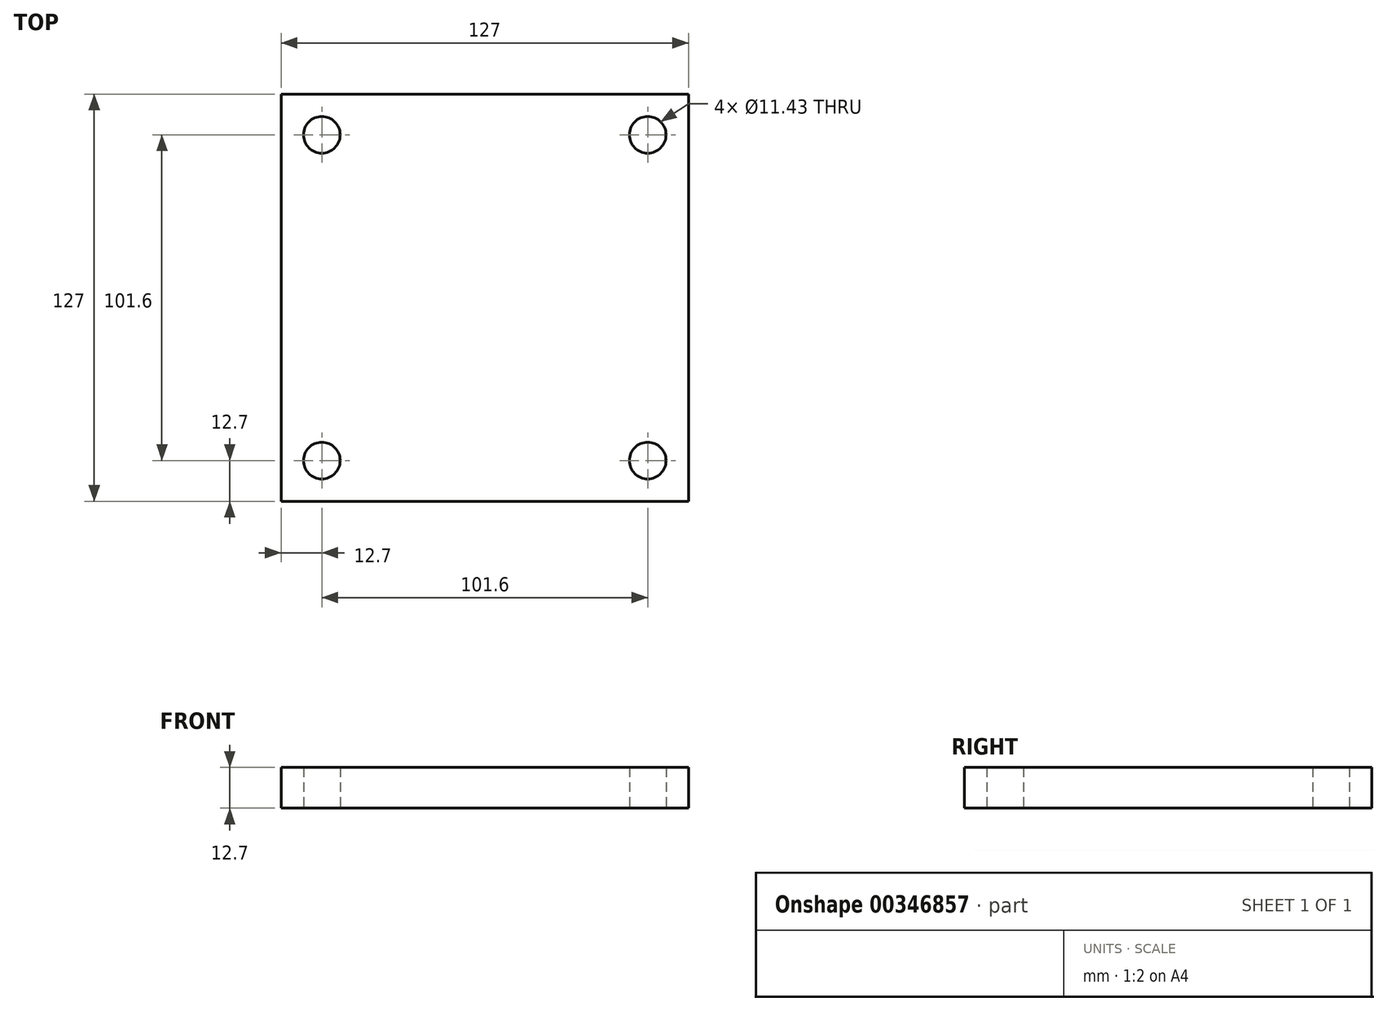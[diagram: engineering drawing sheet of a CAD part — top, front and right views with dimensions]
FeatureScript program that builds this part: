
annotation { "Feature Type Name" : "Feature", "Feature Type Description" : "" }
export const myFeature = defineFeature(function(context is Context, id is Id, definition is map)
    precondition{}
    {
        {
            var Q0;
            Q0=qCreatedBy(makeId("Top.planeOp"),FACE);
            var sketch = newSketch(context, id + "F0", { "sketchPlane" : qUnion([Q0])});
            skLineSegment(sketch, "E0.bottom", {"start": v(63.5, 63.5) * mm, "end": v(-63.5, 63.5) * mm});
            skLineSegment(sketch, "E0.top", {"start": v(63.5, -63.5) * mm, "end": v(-63.5, -63.5) * mm});
            skLineSegment(sketch, "E0.left", {"start": v(63.5, 63.5) * mm, "end": v(63.5, -63.5) * mm});
            skLineSegment(sketch, "E0.right", {"start": v(-63.5, 63.5) * mm, "end": v(-63.5, -63.5) * mm});
            skPoint(sketch, "E0.middle", {"position": v(0, 0) * mm});
            skLineSegment(sketch, "E1.bottom", {"start": v(50.8, 50.8) * mm, "end": v(-50.8, 50.8) * mm});
            skLineSegment(sketch, "E1.top", {"start": v(50.8, -50.8) * mm, "end": v(-50.8, -50.8) * mm});
            skLineSegment(sketch, "E1.left", {"start": v(50.8, 50.8) * mm, "end": v(50.8, -50.8) * mm});
            skLineSegment(sketch, "E1.right", {"start": v(-50.8, 50.8) * mm, "end": v(-50.8, -50.8) * mm});
            skCircle(sketch, "E2", {"center": v(-50.8, 50.8) * mm, "radius": 5.72 * mm});
            skCircle(sketch, "E3", {"center": v(50.8, 50.8) * mm, "radius": 5.72 * mm});
            skCircle(sketch, "E4", {"center": v(50.8, -50.8) * mm, "radius": 5.72 * mm});
            skCircle(sketch, "E5", {"center": v(-50.8, -50.8) * mm, "radius": 5.72 * mm});
            skSolve(sketch);
        }
        {
            var Q0;
            Q0=sQuery(id+"F0.wireOp",EDGE,"E2");
            var Q1;
            Q1=sQuery(id+"F0.wireOp",EDGE,"E3");
            var Q2;
            Q2=sQuery(id+"F0.wireOp",EDGE,"E4");
            var Q3;
            Q3=sQuery(id+"F0.wireOp",EDGE,"E5");
            extrude(context, id + "F1", {"bodyType" : ToolBodyType.SURFACE, "surfaceEntities" : qUnion([Q0, Q1, Q2, Q3]), "depth" : 127 * mm});
        }
        {
            var Q0;
            Q0=makeQuery(id+"F0.imprint","IMPRINT",FACE,{"disambiguationData":[TD([[makeQuery(id+"F0.imprint","IMPRINT",EDGE,{"derivedFrom":sQuery(id+"F0.wireOp",EDGE,"E0.bottom")}),1.0]])]});
            var Q1;
            {var subQ5=sQuery(id+"F0.wireOp",EDGE,"E3");var subQ13=sQuery(id+"F0.wireOp",EDGE,"E1.bottom");var subQ14=makeQuery(id+"F0.imprint","INTERSECT",VERTEX,{"derivedFrom":[subQ13,subQ5]});Q1=makeQuery(id+"F0.imprint","IMPRINT",FACE,{"disambiguationData":[TD([[makeQuery(id+"F0.imprint","IMPRINT",EDGE,{"disambiguationData":[TD([[subQ14,-1.0]])],"derivedFrom":subQ13}),1.0]])]});}
            extrude(context, id + "F2", {"entities" : qUnion([Q0, Q1]), "depth" : 12.7 * mm});
        }
    });
